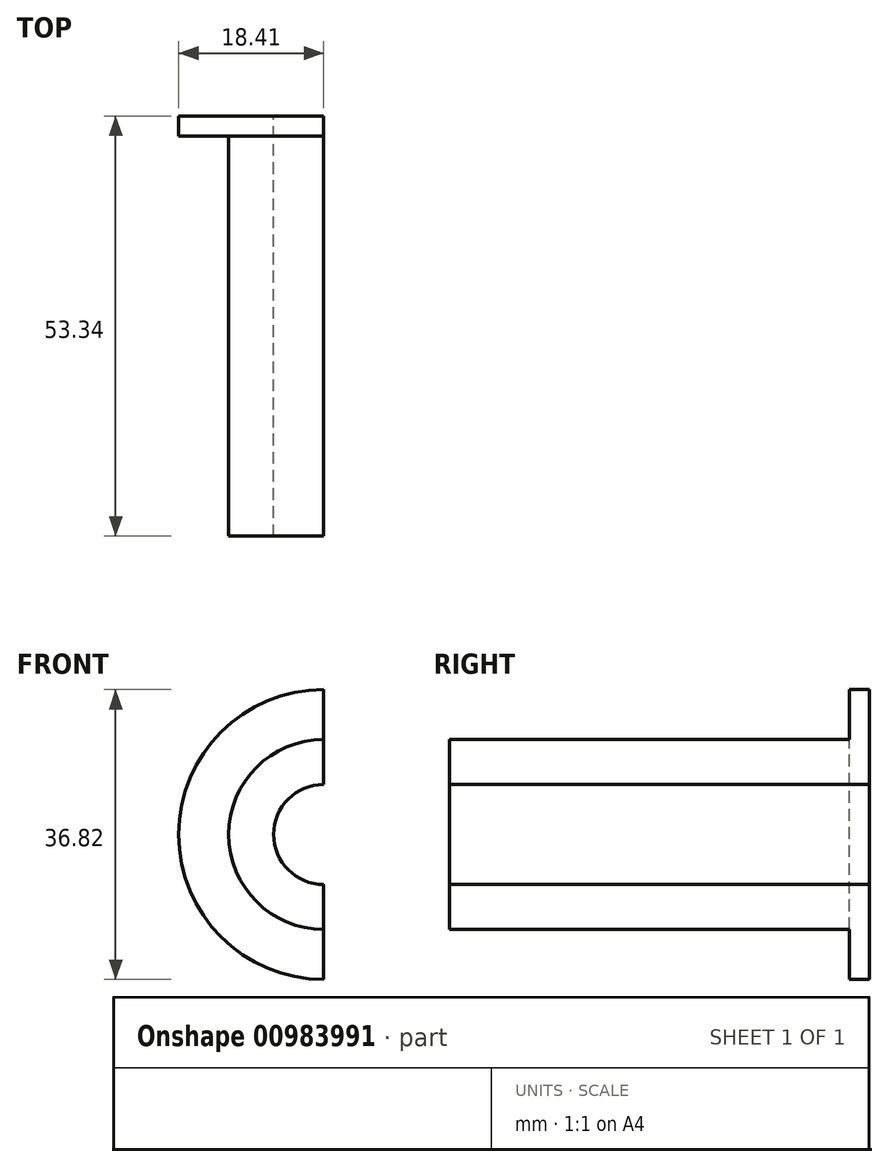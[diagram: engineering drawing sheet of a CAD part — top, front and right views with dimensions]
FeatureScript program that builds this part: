
annotation { "Feature Type Name" : "Feature", "Feature Type Description" : "" }
export const myFeature = defineFeature(function(context is Context, id is Id, definition is map)
    precondition{}
    {
        {
            var Q0;
            Q0=qCreatedBy(makeId("Top.planeOp"),FACE);
            var sketch = newSketch(context, id + "F0", { "sketchPlane" : qUnion([Q0])});
            skLineSegment(sketch, "E0", {"start": v(0, -15.61) * mm, "end": v(12.07, -15.61) * mm});
            skLineSegment(sketch, "E1", {"start": v(12.07, -15.61) * mm, "end": v(12.07, 35.19) * mm});
            skLineSegment(sketch, "E2", {"start": v(12.07, 35.19) * mm, "end": v(18.41, 35.19) * mm});
            skLineSegment(sketch, "E3", {"start": v(18.41, 35.19) * mm, "end": v(18.41, 37.73) * mm});
            skLineSegment(sketch, "E4", {"start": v(18.41, 37.73) * mm, "end": v(0, 37.73) * mm});
            skLineSegment(sketch, "E5", {"start": v(0, 37.73) * mm, "end": v(0, -15.61) * mm});
            skSolve(sketch);
        }
        {
            var Q0;
            Q0=makeQuery(id+"F0.imprint","IMPRINT",FACE,{"disambiguationData":[TD([[makeQuery(id+"F0.imprint","IMPRINT",EDGE,{"derivedFrom":sQuery(id+"F0.wireOp",EDGE,"E0")}),1.0]])]});
            var Q1;
            Q1=sQuery(id+"F0.wireOp",EDGE,"E5");
            revolve(context, id + "F1", {"surfaceOperationType" : NewSurfaceOperationType.NEW, "entities" : qUnion([Q0]), "axis" : qUnion([Q1]), "revolveType" : RevolveType.FULL});
        }
        {
            var Q0;
            Q0=makeQuery(id+"F1.opRevolve","SWEPT_FACE",FACE,{"disambiguationData":[OSD([sQuery(id+"F0.wireOp",EDGE,"E4")])]});
            var sketch = newSketch(context, id + "F2", { "sketchPlane" : qUnion([Q0])});
            skCircle(sketch, "E6", {"center": v(0, 0) * mm, "radius": 6.35 * mm});
            skSolve(sketch);
        }
        {
            var Q0;
            Q0=qSketchRegion(id+"F2",true);
            extrude(context, id + "F3", {"entities" : qUnion([Q0]), "operationType" : NewBodyOperationType.REMOVE, "oppositeDirection" : true, "depth" : 101.6 * mm, "offsetDistance" : 25.4 * mm});
        }
        {
            var Q0;
            Q0=makeQuery(id+"F1.opRevolve","SWEPT_FACE",FACE,{"disambiguationData":[OSD([sQuery(id+"F0.wireOp",EDGE,"E4")])]});
            var sketch = newSketch(context, id + "F4", { "sketchPlane" : qUnion([Q0])});
            skLineSegment(sketch, "E7", {"start": v(0, 18.86) * mm, "end": v(0, 18.41) * mm});
            skLineSegment(sketch, "E8", {"start": v(0, 18.86) * mm, "end": v(0, -20.1) * mm});
            skLineSegment(sketch, "E9", {"start": v(0, -20.1) * mm, "end": v(-23.92, -16.78) * mm});
            skLineSegment(sketch, "E10", {"start": v(-23.92, -16.78) * mm, "end": v(-18.05, 25.6) * mm});
            skLineSegment(sketch, "E11", {"start": v(-18.05, 25.6) * mm, "end": v(0, 32.27) * mm});
            skLineSegment(sketch, "E12", {"start": v(0, 32.27) * mm, "end": v(0, 18.86) * mm});
            skSolve(sketch);
        }
        {
            var Q0;
            Q0 = qSketchRegion(id + "F4", true);
            extrude(context, id + "F5", {"entities" : qUnion([Q0]), "operationType" : NewBodyOperationType.REMOVE, "oppositeDirection" : true, "depth" : 127 * mm, "offsetDistance" : 25.4 * mm});
        }
    });
